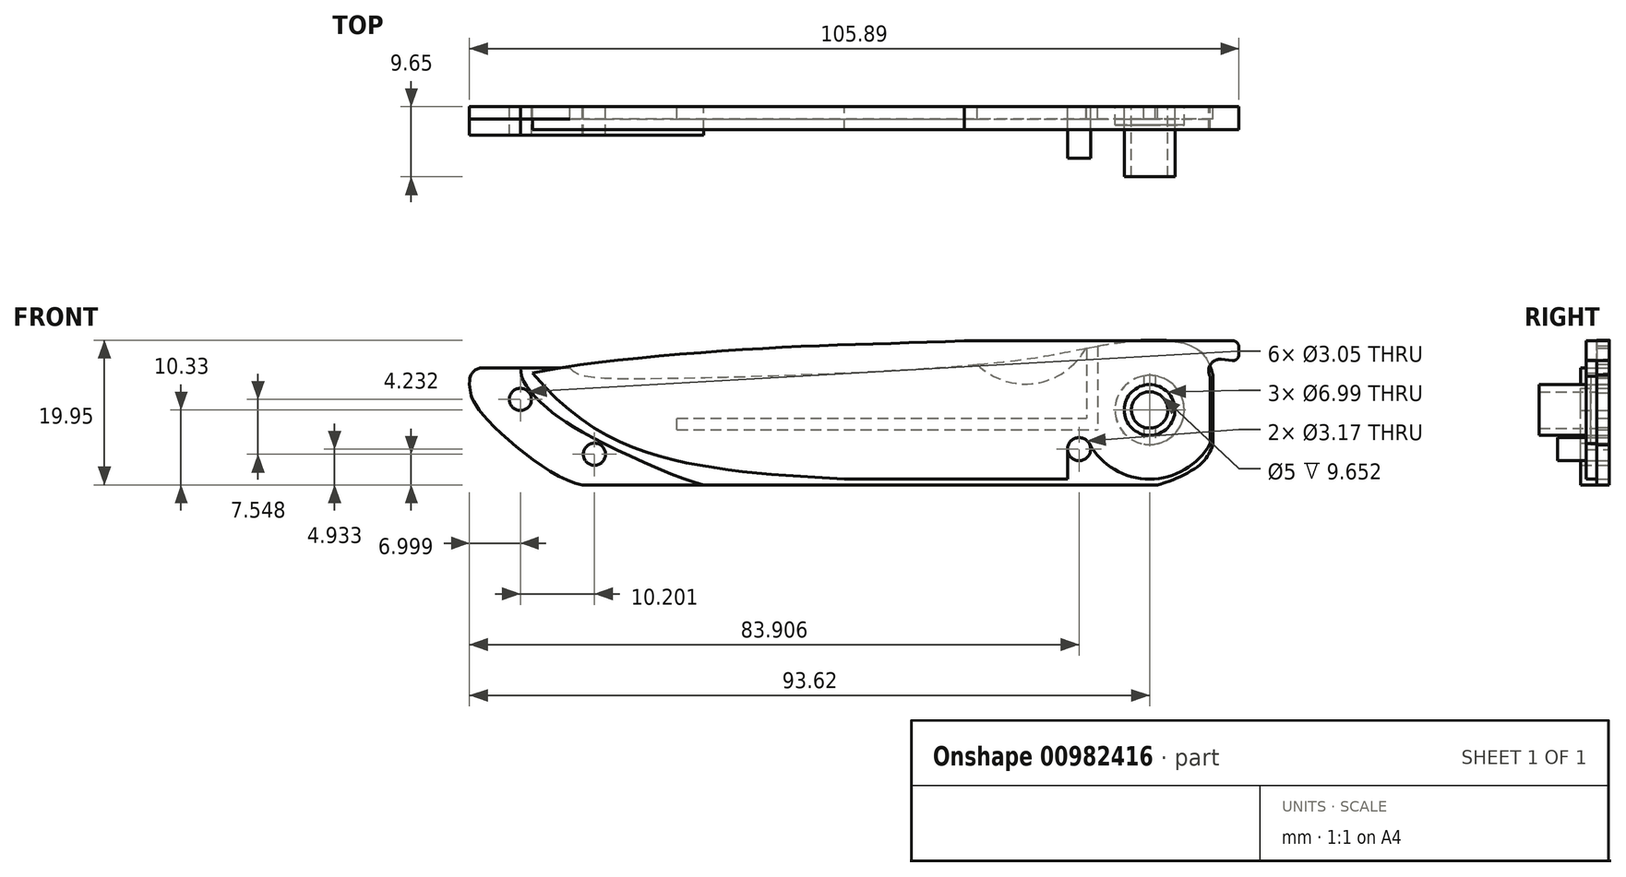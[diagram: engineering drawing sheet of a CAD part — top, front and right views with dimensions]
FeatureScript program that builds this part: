
annotation { "Feature Type Name" : "Feature", "Feature Type Description" : "" }
export const myFeature = defineFeature(function(context is Context, id is Id, definition is map)
    precondition{}
    {
        {
            var Q0;
            Q0=qCreatedBy(makeId("Front.planeOp"),FACE);
            var sketch = newSketch(context, id + "F0", { "sketchPlane" : qUnion([Q0])});
            skCircle(sketch, "E0", {"center": v(0, 0) * mm, "radius": 3.5 * mm});
            skCircle(sketch, "E1", {"center": v(0, 0) * mm, "radius": 2.5 * mm});
            skCircle(sketch, "E2", {"center": v(0, 0) * mm, "radius": 4.76 * mm});
            skLineSegment(sketch, "E3", {"start": v(0, 0) * mm, "end": v(0, 4.76) * mm, "construction": true});
            skLineSegment(sketch, "E4", {"start": v(-0.79, 4.7) * mm, "end": v(-0.79, -4.7) * mm});
            skLineSegment(sketch, "E5.MirrorCS", {"start": v(0.79, 4.7) * mm, "end": v(0.79, -4.7) * mm});
            skArc(sketch, "E6", {"start": v(-8.33, -4.63) * mm, "mid": v(0, -9.53) * mm, "end": v(8.33, -4.63) * mm});
            skLineSegment(sketch, "E7", {"start": v(-11.3, -9.53) * mm, "end": v(-42.03, -9.53) * mm});
            skLineSegment(sketch, "E8", {"start": v(-25.5, 9.53) * mm, "end": v(11.47, 9.53) * mm});
            skLineSegment(sketch, "E9", {"start": v(-14.75, -3.81) * mm, "end": v(-9.71, -3.81) * mm});
            skArc(sketch, "E10", {"start": v(-8.33, -4.63) * mm, "mid": v(-10.14, -3.87) * mm, "end": v(-11.3, -5.45) * mm});
            skLineSegment(sketch, "E11", {"start": v(-11.3, -5.45) * mm, "end": v(-11.3, -9.53) * mm});
            skLineSegment(sketch, "E12", {"start": v(-9.71, -5.4) * mm, "end": v(0, 0) * mm, "construction": true});
            skLineSegment(sketch, "E13", {"start": v(0, 0) * mm, "end": v(-5.25, 9.44) * mm, "construction": true});
            skArc(sketch, "E14.MirrorCS", {"start": v(8.33, 4.63) * mm, "mid": v(8.4, 6.28) * mm, "end": v(9.89, 6.98) * mm});
            skPoint(sketch, "E15.orphan", {"position": v(0, -9.53) * mm});
            skPoint(sketch, "E16.orphan", {"position": v(-11.3, -11.19) * mm});
            skLineSegment(sketch, "E17", {"start": v(12.27, 7.6) * mm, "end": v(12.27, 8.72) * mm});
            skPoint(sketch, "E18.orphan", {"position": v(9.14, 9.52) * mm});
            skPoint(sketch, "E19.orphan", {"position": v(15.47, 3.69) * mm});
            skPoint(sketch, "E20.MirrorCS.start.orphan", {"position": v(10.6, 6.71) * mm});
            skLineSegment(sketch, "E21", {"start": v(11.38, 6.81) * mm, "end": v(9.89, 6.98) * mm});
            skArc(sketch, "E22", {"start": v(11.38, 6.81) * mm, "mid": v(12, 7.01) * mm, "end": v(12.27, 7.6) * mm});
            skArc(sketch, "E23", {"start": v(12.27, 8.72) * mm, "mid": v(12.03, 9.3) * mm, "end": v(11.47, 9.52) * mm});
            skPoint(sketch, "E24.orphan", {"position": v(12.27, 9.52) * mm});
            skFitSpline(sketch, "E25", {"points": [v(-84.94, 5.11) * mm, v(-64.38, -7.13) * mm, v(-42.03, -9.53) * mm], "startDerivative": vector(37.68, -45.65) * mm, "endDerivative": vector(46.54, -2.84) * mm});
            skFitSpline(sketch, "E26", {"points": [v(-84.94, 5.11) * mm, v(-53.91, 8.44) * mm, v(-25.5, 9.52) * mm], "startDerivative": vector(42.66, 8.99) * mm, "endDerivative": vector(60.72, 2.46) * mm});
            skCircle(sketch, "E27", {"center": v(-9.71, -5.4) * mm, "radius": 1.59 * mm});
            skLineSegment(sketch, "E28", {"start": v(8.33, 4.63) * mm, "end": v(8.33, -4.63) * mm});
            skSolve(sketch);
        }
        {
            var Q0;
            Q0=makeQuery(id+"F0.imprint","IMPRINT",FACE,{"disambiguationData":[TD([[makeQuery(id+"F0.imprint","IMPRINT",EDGE,{"derivedFrom":sQuery(id+"F0.wireOp",EDGE,"E0")}),1.0]])]});
            extrude(context, id + "F1", {"entities" : qUnion([Q0]), "depth" : 9.65 * mm, "offsetDistance" : 25.4 * mm});
        }
        {
            var Q0;
            Q0=makeQuery(id+"F0.imprint","IMPRINT",FACE,{"disambiguationData":[TD([[makeQuery(id+"F0.imprint","IMPRINT",EDGE,{"derivedFrom":sQuery(id+"F0.wireOp",EDGE,"E0")}),-1.0]])]});
            extrude(context, id + "F2", {"entities" : qUnion([Q0]), "operationType" : NewBodyOperationType.ADD, "depth" : 2.54 * mm, "offsetDistance" : 25.4 * mm});
        }
        {
            var Q0;
            {var subQ0=sQuery(id+"F0.wireOp",EDGE,"E4");var subQ1=sQuery(id+"F0.wireOp",EDGE,"E0");var subQ2=makeQuery(id+"F0.imprint","INTERSECT",VERTEX,{"disambiguationData":[OD(0.0)],"derivedFrom":[subQ1,subQ0]});Q0=makeQuery(id+"F0.imprint","IMPRINT",FACE,{"disambiguationData":[TD([[makeQuery(id+"F0.imprint","IMPRINT",EDGE,{"disambiguationData":[TD([[subQ2,1.0]])],"derivedFrom":subQ1}),-1.0]])]});}
            var Q1;
            {var subQ0=sQuery(id+"F0.wireOp",EDGE,"E4");var subQ1=sQuery(id+"F0.wireOp",EDGE,"E0");var subQ2=makeQuery(id+"F0.imprint","INTERSECT",VERTEX,{"disambiguationData":[OD(1.0)],"derivedFrom":[subQ1,subQ0]});Q1=makeQuery(id+"F0.imprint","IMPRINT",FACE,{"disambiguationData":[TD([[makeQuery(id+"F0.imprint","IMPRINT",EDGE,{"disambiguationData":[TD([[subQ2,-1.0]])],"derivedFrom":subQ1}),-1.0]])]});}
            var Q2;
            {var subQ0=sQuery(id+"F0.wireOp",EDGE,"E4");var subQ1=sQuery(id+"F0.wireOp",EDGE,"E0");var subQ2=makeQuery(id+"F0.imprint","INTERSECT",VERTEX,{"disambiguationData":[OD(0.0)],"derivedFrom":[subQ1,subQ0]});Q2=makeQuery(id+"F0.imprint","IMPRINT",FACE,{"disambiguationData":[TD([[makeQuery(id+"F0.imprint","IMPRINT",EDGE,{"disambiguationData":[TD([[subQ2,1.0]])],"derivedFrom":subQ1}),1.0]])]});}
            var Q3;
            {var subQ0=sQuery(id+"F0.wireOp",EDGE,"E4");var subQ1=sQuery(id+"F0.wireOp",EDGE,"E0");var subQ2=makeQuery(id+"F0.imprint","INTERSECT",VERTEX,{"disambiguationData":[OD(1.0)],"derivedFrom":[subQ1,subQ0]});Q3=makeQuery(id+"F0.imprint","IMPRINT",FACE,{"disambiguationData":[TD([[makeQuery(id+"F0.imprint","IMPRINT",EDGE,{"disambiguationData":[TD([[subQ2,-1.0]])],"derivedFrom":subQ1}),1.0]])]});}
            extrude(context, id + "F3", {"entities" : qUnion([Q0, Q1, Q2, Q3]), "operationType" : NewBodyOperationType.REMOVE, "depth" : 1.7 * mm, "offsetDistance" : 25.4 * mm});
        }
        {
            var Q0;
            {var subQ9=sQuery(id+"F0.wireOp",EDGE,"E6");Q0=makeQuery(id+"F0.imprint","IMPRINT",FACE,{"disambiguationData":[TD([[makeQuery(id+"F0.imprint","IMPRINT",EDGE,{"derivedFrom":subQ9}),1.0]])]});}
            var Q1;
            {var subQ0=sQuery(id+"F0.wireOp",EDGE,"E5.MirrorCS");var subQ1=sQuery(id+"F0.wireOp",EDGE,"E0");var subQ2=makeQuery(id+"F0.imprint","INTERSECT",VERTEX,{"disambiguationData":[OD(0.0)],"derivedFrom":[subQ1,subQ0]});Q1=makeQuery(id+"F0.imprint","IMPRINT",FACE,{"disambiguationData":[TD([[makeQuery(id+"F0.imprint","IMPRINT",EDGE,{"disambiguationData":[TD([[subQ2,1.0]])],"derivedFrom":subQ1}),-1.0]])]});}
            var Q2;
            {var subQ0=sQuery(id+"F0.wireOp",EDGE,"E4");var subQ1=sQuery(id+"F0.wireOp",EDGE,"E0");var subQ2=makeQuery(id+"F0.imprint","INTERSECT",VERTEX,{"disambiguationData":[OD(0.0)],"derivedFrom":[subQ1,subQ0]});Q2=makeQuery(id+"F0.imprint","IMPRINT",FACE,{"disambiguationData":[TD([[makeQuery(id+"F0.imprint","IMPRINT",EDGE,{"disambiguationData":[TD([[subQ2,1.0]])],"derivedFrom":subQ1}),-1.0]])]});}
            var Q3;
            {var subQ0=sQuery(id+"F0.wireOp",EDGE,"E4");var subQ1=sQuery(id+"F0.wireOp",EDGE,"E0");var subQ2=makeQuery(id+"F0.imprint","INTERSECT",VERTEX,{"disambiguationData":[OD(0.0)],"derivedFrom":[subQ1,subQ0]});Q3=makeQuery(id+"F0.imprint","IMPRINT",FACE,{"disambiguationData":[TD([[makeQuery(id+"F0.imprint","IMPRINT",EDGE,{"disambiguationData":[TD([[subQ2,-1.0]])],"derivedFrom":subQ1}),-1.0]])]});}
            var Q4;
            {var subQ0=sQuery(id+"F0.wireOp",EDGE,"E4");var subQ1=sQuery(id+"F0.wireOp",EDGE,"E0");var subQ2=makeQuery(id+"F0.imprint","INTERSECT",VERTEX,{"disambiguationData":[OD(1.0)],"derivedFrom":[subQ1,subQ0]});Q4=makeQuery(id+"F0.imprint","IMPRINT",FACE,{"disambiguationData":[TD([[makeQuery(id+"F0.imprint","IMPRINT",EDGE,{"disambiguationData":[TD([[subQ2,-1.0]])],"derivedFrom":subQ1}),-1.0]])]});}
            extrude(context, id + "F4", {"entities" : qUnion([Q0, Q1, Q2, Q3, Q4]), "depth" : 3.17 * mm, "offsetDistance" : 25.4 * mm});
        }
        {
            var Q0;
            Q0=qCreatedBy(makeId("Front.planeOp"),FACE);
            var sketch = newSketch(context, id + "F5", { "sketchPlane" : qUnion([Q0])});
            skCircle(sketch, "E29", {"center": v(0, 0) * mm, "radius": 3.5 * mm});
            skCircle(sketch, "E30", {"center": v(-9.71, -5.4) * mm, "radius": 1.59 * mm});
            skLineSegment(sketch, "E31", {"start": v(8.7, 4.83) * mm, "end": v(8.7, -4.82) * mm});
            skLineSegment(sketch, "E32", {"start": v(1.12, -10.33) * mm, "end": v(-78.09, -10.33) * mm});
            skLineSegment(sketch, "E33", {"start": v(-91.8, 5.8) * mm, "end": v(-79.82, 5.8) * mm});
            skFitSpline(sketch, "E34", {"points": [v(-79.82, 5.8) * mm, v(-70.17, 4.34) * mm, v(-19.3, 6.72) * mm, v(-5.54, 9.09) * mm, v(5.75, 8.83) * mm, v(8.7, 4.83) * mm], "startDerivative": vector(15.63, -25.43) * mm, "endDerivative": vector(11.45, -45.8) * mm});
            skFitSpline(sketch, "E35", {"points": [v(8.7, -4.82) * mm, v(6.46, -7.91) * mm, v(1.12, -10.33) * mm, v(1, -10.33) * mm], "startDerivative": vector(-3.14, -7.82) * mm, "endDerivative": vector(-0.89, 0.23) * mm});
            skFitSpline(sketch, "E36", {"points": [v(-78.09, -10.33) * mm, v(-92.15, -0.16) * mm, v(-93.51, 2.57) * mm, v(-93.44, 5.8) * mm], "startDerivative": vector(-24.96, 4.28) * mm, "endDerivative": vector(3.24, 23.29) * mm});
            skLineSegment(sketch, "E37.MirrorCS", {"start": v(-8.7, 8.52) * mm, "end": v(-8.7, -1.13) * mm});
            skPoint(sketch, "E38.orphan", {"position": v(-8.7, 4.83) * mm});
            skLineSegment(sketch, "E39", {"start": v(-65.07, -1.13) * mm, "end": v(-8.7, -1.13) * mm});
            skPoint(sketch, "E40.trimOffspring.end.orphan", {"position": v(-8.7, -4.82) * mm});
            skFitSpline(sketch, "E41", {"points": [v(-61.37, -10.33) * mm, v(-76.88, -3.7) * mm, v(-83.17, 0.48) * mm, v(-86.21, 4.05) * mm, v(-86.63, 5.8) * mm], "startDerivative": vector(-26.46, 5.94) * mm, "endDerivative": vector(-1.4, 10.38) * mm});
            skArc(sketch, "E42", {"start": v(-91.8, 5.8) * mm, "mid": v(-93.06, 5.3) * mm, "end": v(-93.61, 4.07) * mm});
            skCircle(sketch, "E43", {"center": v(-86.62, 1.45) * mm, "radius": 1.52 * mm});
            skCircle(sketch, "E44", {"center": v(-76.42, -6.1) * mm, "radius": 1.52 * mm});
            skLineSegment(sketch, "E45.0", {"start": v(-65.07, -2.7) * mm, "end": v(-7.13, -2.7) * mm});
            skLineSegment(sketch, "E46.0", {"start": v(-7.13, 8.82) * mm, "end": v(-7.13, -2.7) * mm});
            skLineSegment(sketch, "E47", {"start": v(-65.07, -2.7) * mm, "end": v(-65.07, -1.13) * mm});
            skLineSegment(sketch, "E48", {"start": v(-8.7, 8.52) * mm, "end": v(-7.13, 8.82) * mm});
            skArc(sketch, "E49", {"start": v(-23.75, 6.27) * mm, "mid": v(-15.7, 3.68) * mm, "end": v(-8.77, 8.5) * mm});
            skSolve(sketch);
        }
        {
            var Q0;
            Q0=makeQuery(id+"F5.imprint","IMPRINT",FACE,{"disambiguationData":[TD([[makeQuery(id+"F5.imprint","IMPRINT",EDGE,{"derivedFrom":sQuery(id+"F5.wireOp",EDGE,"E29")}),-1.0]])]});
            var Q1;
            {var subQ1=sQuery(id+"F5.wireOp",EDGE,"E36");Q1=makeQuery(id+"F5.imprint","IMPRINT",FACE,{"disambiguationData":[TD([[makeQuery(id+"F5.imprint","IMPRINT",EDGE,{"derivedFrom":subQ1}),-1.0]])]});}
            var Q2;
            {var subQ0=sQuery(id+"F5.wireOp",EDGE,"E49");Q2=makeQuery(id+"F5.imprint","IMPRINT",FACE,{"disambiguationData":[TD([[makeQuery(id+"F5.imprint","IMPRINT",EDGE,{"derivedFrom":subQ0}),1.0]])]});}
            extrude(context, id + "F6", {"entities" : qUnion([Q0, Q1, Q2]), "depth" : 1.7 * mm, "offsetDistance" : 25.4 * mm});
        }
        {
            var Q0;
            Q0=makeQuery(id+"F5.imprint","IMPRINT",FACE,{"disambiguationData":[TD([[makeQuery(id+"F5.imprint","IMPRINT",EDGE,{"derivedFrom":sQuery(id+"F5.wireOp",EDGE,"E30")}),1.0]])]});
            extrude(context, id + "F7", {"entities" : qUnion([Q0]), "depth" : 7.11 * mm, "offsetDistance" : 25.4 * mm});
        }
        {
            var Q0;
            {var subQ1=sQuery(id+"F5.wireOp",EDGE,"E36");Q0=makeQuery(id+"F5.imprint","IMPRINT",FACE,{"disambiguationData":[TD([[makeQuery(id+"F5.imprint","IMPRINT",EDGE,{"derivedFrom":subQ1}),-1.0]])]});}
            extrude(context, id + "F8", {"entities" : qUnion([Q0]), "depth" : 3.94 * mm, "offsetDistance" : 25.4 * mm});
        }
        {
            var Q0;
            Q0=makeQuery(id+"F5.imprint","IMPRINT",FACE,{"disambiguationData":[TD([[makeQuery(id+"F5.imprint","IMPRINT",EDGE,{"derivedFrom":sQuery(id+"F5.wireOp",EDGE,"E29")}),-1.0]])]});
            var Q1;
            Q1=makeQuery(id+"F5.imprint","IMPRINT",FACE,{"disambiguationData":[TD([[makeQuery(id+"F5.imprint","IMPRINT",EDGE,{"derivedFrom":sQuery(id+"F5.wireOp",EDGE,"E37.MirrorCS")}),1.0]])]});
            var Q2;
            {var subQ1=sQuery(id+"F5.wireOp",EDGE,"E36");Q2=makeQuery(id+"F5.imprint","IMPRINT",FACE,{"disambiguationData":[TD([[makeQuery(id+"F5.imprint","IMPRINT",EDGE,{"derivedFrom":subQ1}),-1.0]])]});}
            extrude(context, id + "F9", {"entities" : qUnion([Q0, Q1, Q2]), "depth" : 1.7 * mm, "offsetDistance" : 25.4 * mm});
        }
    });
